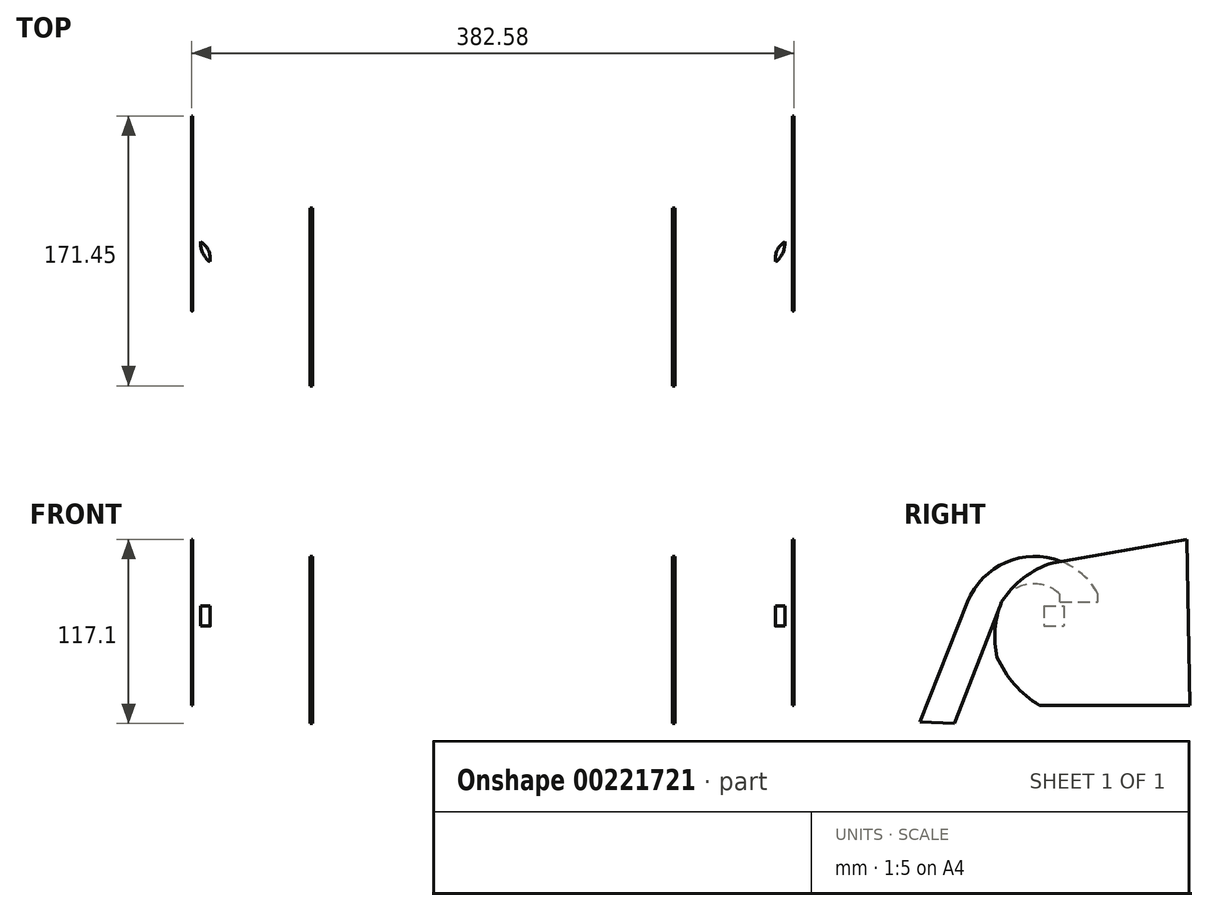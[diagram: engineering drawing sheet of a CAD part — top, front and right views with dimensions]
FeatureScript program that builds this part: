
annotation { "Feature Type Name" : "Feature", "Feature Type Description" : "" }
export const myFeature = defineFeature(function(context is Context, id is Id, definition is map)
    precondition{}
    {
        {
            var Q0;
            Q0=qCreatedBy(makeId("Right.planeOp"),FACE);
            var sketch = newSketch(context, id + "F0", { "sketchPlane" : qUnion([Q0])});
            skFitSpline(sketch, "E0", {"points": [v(37.4, 30.18) * mm, v(-5.8, 5.18) * mm, v(-40.32, 0) * mm, v(-45.03, -6.44) * mm, v(-9.82, -4.68) * mm, v(37.4, 30.18) * mm]});
            skSolve(sketch);
        }
        {
            var Q0;
            Q0=sQuery(id+"F0.wireOp",EDGE,"E0");
            extrude(context, id + "F1", {"bodyType" : ToolBodyType.SURFACE, "surfaceEntities" : qUnion([Q0]), "depth" : 381 * mm});
        }
        {
            var Q0;
            Q0=qCreatedBy(makeId("Top.planeOp"),FACE);
            var sketch = newSketch(context, id + "F2", { "sketchPlane" : qUnion([Q0])});
            skArc(sketch, "E1", {"start": v(5, -30.59) * mm, "mid": v(6.3, -37.73) * mm, "end": v(10.83, -43.4) * mm});
            skArc(sketch, "E2", {"start": v(10.83, -43.4) * mm, "mid": v(9.86, -36.11) * mm, "end": v(5, -30.59) * mm});
            skSolve(sketch);
        }
        {
            var Q0;
            Q0 = qSketchRegion(id + "F2", true);
            extrude(context, id + "F3", {"entities" : qUnion([Q0]), "depth" : 12.7 * mm});
        }
        {
            var Q0;
            Q0=makeQuery(id+"F3.opExtrude","SWEPT_BODY",BODY,{"disambiguationData":[OSD([sQuery(id+"F2.wireOp",EDGE,"E1"),sQuery(id+"F2.wireOp",EDGE,"E2")])]});
            var Q1;
            Q1=qCreatedBy(makeId("Top.planeOp"),FACE);
            transform(context, id + "F4", {"entities" : qUnion([Q0]), "transformType" : TransformType.TRANSLATION_DISTANCE, "transformDirection" : qUnion([Q1]), "distance" : 15.24 * mm, "oppositeDirection" : true, "makeCopy" : false});
        }
        {
            var Q0;
            Q0=makeQuery(id+"F1.opExtrude","SWEPT_BODY",BODY,{"disambiguationData":[OSD([sQuery(id+"F0.wireOp",EDGE,"E0")])]});
            var Q1;
            Q1=makeQuery(id+"F3.opExtrude","SWEPT_BODY",BODY,{"disambiguationData":[OSD([sQuery(id+"F2.wireOp",EDGE,"E1"),sQuery(id+"F2.wireOp",EDGE,"E2")])]});
            var Q2;
            Q2=qCreatedBy(makeId("Right.planeOp"),FACE);
            transform(context, id + "F5", {"entities" : qUnion([Q0, Q1]), "transformType" : TransformType.TRANSLATION_DISTANCE, "transformDirection" : qUnion([Q2]), "distance" : 190.5 * mm, "oppositeDirection" : true, "makeCopy" : false});
        }
        {
            var Q0;
            Q0=makeQuery(id+"F3.opExtrude","SWEPT_BODY",BODY,{"disambiguationData":[OSD([sQuery(id+"F2.wireOp",EDGE,"E1"),sQuery(id+"F2.wireOp",EDGE,"E2")])]});
            var Q1;
            Q1=qCreatedBy(makeId("Right.planeOp"),FACE);
            mirror(context, id + "F6", {"entities" : qUnion([Q0]), "mirrorPlane" : qUnion([Q1])});
        }
        {
            var Q0;
            Q0=qCreatedBy(makeId("Right.planeOp"),FACE);
            var sketch = newSketch(context, id + "F7", { "sketchPlane" : qUnion([Q0])});
            skLineSegment(sketch, "E3", {"start": v(47.24, 39.88) * mm, "end": v(49.28, -65.53) * mm});
            skLineSegment(sketch, "E4", {"start": v(49.28, -65.53) * mm, "end": v(-46.23, -65.53) * mm});
            skArc(sketch, "E5", {"start": v(-73.15, -35.05) * mm, "mid": v(-62.05, -52.37) * mm, "end": v(-46.23, -65.53) * mm});
            skArc(sketch, "E6", {"start": v(-70.36, 0) * mm, "mid": v(-74.38, -17.32) * mm, "end": v(-73.15, -35.05) * mm});
            skArc(sketch, "E7", {"start": v(-37.85, 24.9) * mm, "mid": v(-56.32, 15.35) * mm, "end": v(-70.36, 0) * mm});
            skLineSegment(sketch, "E8", {"start": v(-37.85, 24.9) * mm, "end": v(47.24, 39.88) * mm});
            skSolve(sketch);
        }
        {
            var Q0;
            Q0=makeQuery(id+"F7.imprint","IMPRINT",FACE,{"disambiguationData":[TD([[makeQuery(id+"F7.imprint","IMPRINT",EDGE,{"derivedFrom":sQuery(id+"F7.wireOp",EDGE,"E3")}),-1.0]])]});
            extrude(context, id + "F8", {"entities" : qUnion([Q0]), "depth" : 0.8 * mm});
        }
        {
            var Q0;
            Q0=makeQuery(id+"F8.opExtrude","SWEPT_BODY",BODY,{"disambiguationData":[OSD([sQuery(id+"F7.wireOp",EDGE,"E3"),sQuery(id+"F7.wireOp",EDGE,"E4"),sQuery(id+"F7.wireOp",EDGE,"E5"),sQuery(id+"F7.wireOp",EDGE,"E6"),sQuery(id+"F7.wireOp",EDGE,"E7"),sQuery(id+"F7.wireOp",EDGE,"E8")])]});
            var Q1;
            Q1=qCreatedBy(makeId("Right.planeOp"),FACE);
            transform(context, id + "F9", {"entities" : qUnion([Q0]), "transformType" : TransformType.TRANSLATION_DISTANCE, "transformDirection" : qUnion([Q1]), "distance" : 190.5 * mm, "makeCopy" : false});
        }
        {
            var Q0;
            Q0=makeQuery(id+"F8.opExtrude","SWEPT_BODY",BODY,{"disambiguationData":[OSD([sQuery(id+"F7.wireOp",EDGE,"E3"),sQuery(id+"F7.wireOp",EDGE,"E4"),sQuery(id+"F7.wireOp",EDGE,"E5"),sQuery(id+"F7.wireOp",EDGE,"E6"),sQuery(id+"F7.wireOp",EDGE,"E7"),sQuery(id+"F7.wireOp",EDGE,"E8")])]});
            var Q1;
            Q1=qCreatedBy(makeId("Right.planeOp"),FACE);
            mirror(context, id + "F10", {"entities" : qUnion([Q0]), "mirrorPlane" : qUnion([Q1])});
        }
        {
            var Q0;
            Q0=qCreatedBy(makeId("Right.planeOp"),FACE);
            var sketch = newSketch(context, id + "F11", { "sketchPlane" : qUnion([Q0])});
            skLineSegment(sketch, "E9", {"start": v(-33.27, 0) * mm, "end": v(-9.14, 0) * mm});
            skLineSegment(sketch, "E10", {"start": v(-9.14, 0) * mm, "end": v(-9.14, 5.28) * mm});
            skArc(sketch, "E11", {"start": v(-9.14, 5.28) * mm, "mid": v(-52.22, 28.87) * mm, "end": v(-91.95, 0) * mm});
            skLineSegment(sketch, "E12", {"start": v(-33.27, 0) * mm, "end": v(-33.27, 4.88) * mm});
            skArc(sketch, "E13", {"start": v(-33.27, 4.88) * mm, "mid": v(-52.88, 11.43) * mm, "end": v(-70.1, 0) * mm});
            skLineSegment(sketch, "E14", {"start": v(-91.95, 0) * mm, "end": v(-122.17, -76.2) * mm});
            skLineSegment(sketch, "E15", {"start": v(-70.1, 0) * mm, "end": v(-100.08, -77.22) * mm});
            skLineSegment(sketch, "E16", {"start": v(-122.17, -76.2) * mm, "end": v(-100.08, -77.22) * mm});
            skSolve(sketch);
        }
        {
            var Q0;
            Q0=makeQuery(id+"F11.imprint","IMPRINT",FACE,{"disambiguationData":[TD([[makeQuery(id+"F11.imprint","IMPRINT",EDGE,{"derivedFrom":sQuery(id+"F11.wireOp",EDGE,"E9")}),1.0]])]});
            extrude(context, id + "F12", {"entities" : qUnion([Q0]), "depth" : 1.59 * mm});
        }
        {
            var Q0;
            Q0=makeQuery(id+"F12.opExtrude","SWEPT_BODY",BODY,{"disambiguationData":[OSD([sQuery(id+"F11.wireOp",EDGE,"E9"),sQuery(id+"F11.wireOp",EDGE,"E10"),sQuery(id+"F11.wireOp",EDGE,"E11"),sQuery(id+"F11.wireOp",EDGE,"E12"),sQuery(id+"F11.wireOp",EDGE,"E13"),sQuery(id+"F11.wireOp",EDGE,"E14"),sQuery(id+"F11.wireOp",EDGE,"E15"),sQuery(id+"F11.wireOp",EDGE,"E16")])]});
            var Q1;
            Q1=qCreatedBy(makeId("Right.planeOp"),FACE);
            transform(context, id + "F13", {"entities" : qUnion([Q0]), "transformType" : TransformType.TRANSLATION_DISTANCE, "transformDirection" : qUnion([Q1]), "distance" : 114.3 * mm, "makeCopy" : false});
        }
        {
            var Q0;
            Q0=makeQuery(id+"F12.opExtrude","SWEPT_BODY",BODY,{"disambiguationData":[OSD([sQuery(id+"F11.wireOp",EDGE,"E9"),sQuery(id+"F11.wireOp",EDGE,"E10"),sQuery(id+"F11.wireOp",EDGE,"E11"),sQuery(id+"F11.wireOp",EDGE,"E12"),sQuery(id+"F11.wireOp",EDGE,"E13"),sQuery(id+"F11.wireOp",EDGE,"E14"),sQuery(id+"F11.wireOp",EDGE,"E15"),sQuery(id+"F11.wireOp",EDGE,"E16")])]});
            var Q1;
            Q1=qCreatedBy(makeId("Right.planeOp"),FACE);
            mirror(context, id + "F14", {"entities" : qUnion([Q0]), "mirrorPlane" : qUnion([Q1])});
        }
    });
